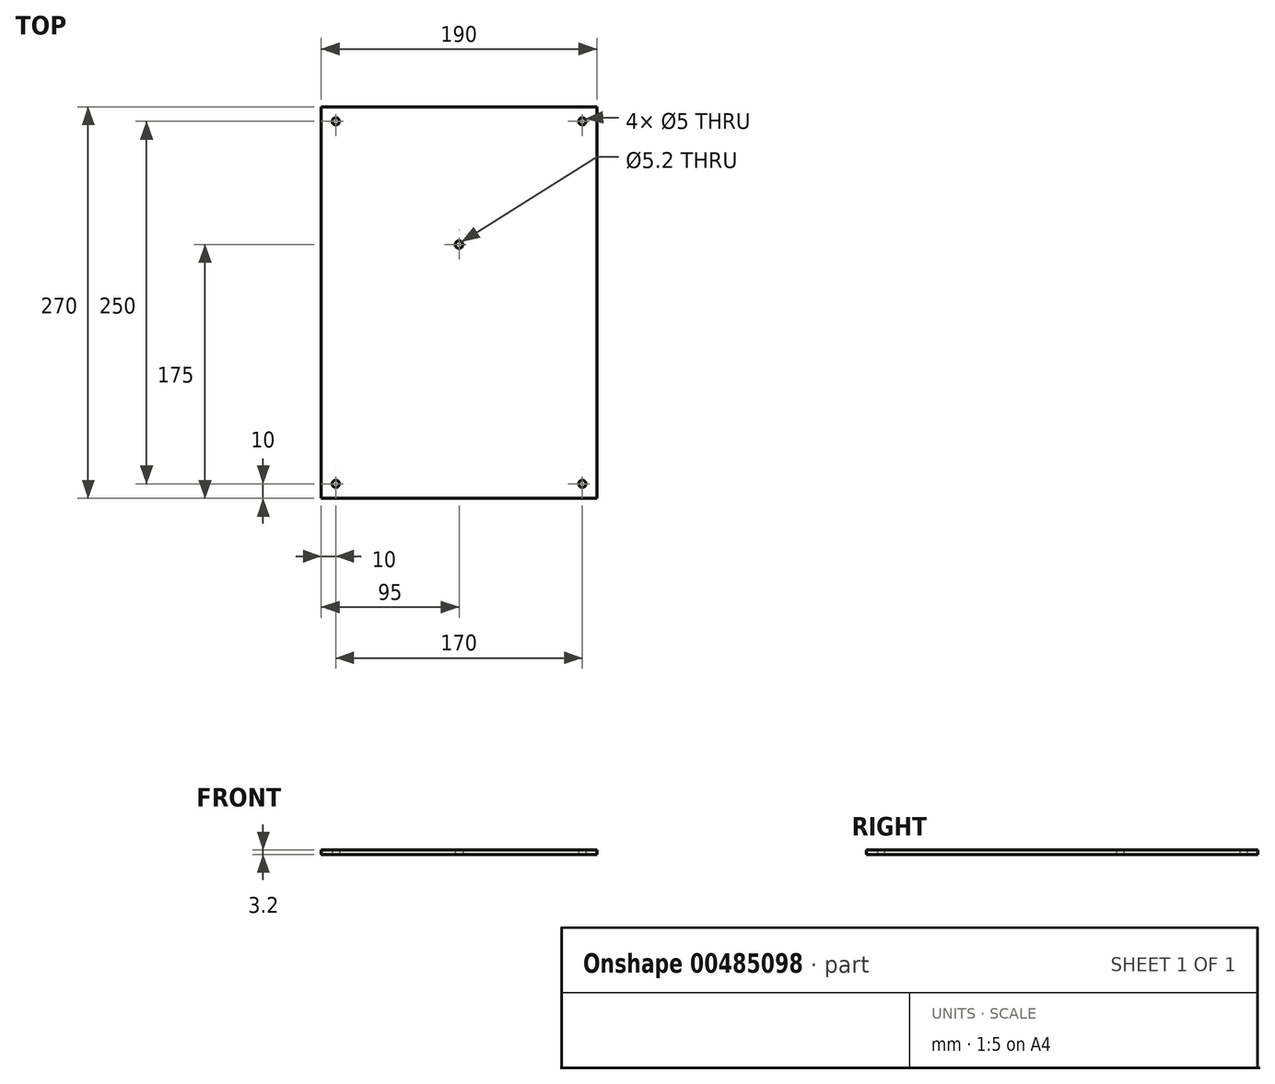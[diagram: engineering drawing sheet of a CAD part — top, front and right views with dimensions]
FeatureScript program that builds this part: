
annotation { "Feature Type Name" : "Feature", "Feature Type Description" : "" }
export const myFeature = defineFeature(function(context is Context, id is Id, definition is map)
    precondition{}
    {
        {
            var Q0;
            Q0=qCreatedBy(makeId("Top.planeOp"),FACE);
            var sketch = newSketch(context, id + "F0", { "sketchPlane" : qUnion([Q0])});
            skLineSegment(sketch, "E0.bottom", {"start": v(-95, 135) * mm, "end": v(95, 135) * mm});
            skLineSegment(sketch, "E0.top", {"start": v(-95, -135) * mm, "end": v(95, -135) * mm});
            skLineSegment(sketch, "E0.left", {"start": v(-95, 135) * mm, "end": v(-95, -135) * mm});
            skLineSegment(sketch, "E0.right", {"start": v(95, 135) * mm, "end": v(95, -135) * mm});
            skPoint(sketch, "E0.middle", {"position": v(0, 0) * mm});
            skCircle(sketch, "E1", {"center": v(-85, -125) * mm, "radius": 2.5 * mm});
            skCircle(sketch, "E2", {"center": v(-85, 125) * mm, "radius": 2.5 * mm});
            skCircle(sketch, "E3", {"center": v(85, 125) * mm, "radius": 2.5 * mm});
            skCircle(sketch, "E4", {"center": v(85, -125) * mm, "radius": 2.5 * mm});
            skLineSegment(sketch, "E5", {"start": v(-95, 40) * mm, "end": v(95, 40) * mm, "construction": true});
            skLineSegment(sketch, "E6", {"start": v(0, 135) * mm, "end": v(0, -135) * mm, "construction": true});
            skCircle(sketch, "E7", {"center": v(0, 40) * mm, "radius": 80 * mm});
            skLineSegment(sketch, "E8", {"start": v(-69.28, 80) * mm, "end": v(69.28, 80) * mm, "construction": true});
            skLineSegment(sketch, "E9", {"start": v(-69.28, 0) * mm, "end": v(69.28, 0) * mm, "construction": true});
            skCircle(sketch, "E10", {"center": v(0, 40) * mm, "radius": 2.6 * mm});
            skSolve(sketch);
        }
        {
            var Q0;
            Q0=makeQuery(id+"F0.imprint","IMPRINT",FACE,{"disambiguationData":[TD([[makeQuery(id+"F0.imprint","IMPRINT",EDGE,{"derivedFrom":sQuery(id+"F0.wireOp",EDGE,"E0.bottom")}),-1.0]])]});
            var Q1;
            Q1=makeQuery(id+"F0.imprint","IMPRINT",FACE,{"disambiguationData":[TD([[makeQuery(id+"F0.imprint","IMPRINT",EDGE,{"derivedFrom":sQuery(id+"F0.wireOp",EDGE,"7sevgCVw-3VQA-PXdj-X2Id-GUKon9O2GLyd")}),1.0]])]});
            var Q2;
            Q2=makeQuery(id+"F0.imprint","IMPRINT",FACE,{"disambiguationData":[TD([[makeQuery(id+"F0.imprint","IMPRINT",EDGE,{"derivedFrom":sQuery(id+"F0.wireOp",EDGE,"E7")}),1.0]])]});
            extrude(context, id + "F1", {"entities" : qUnion([Q0, Q1, Q2]), "depth" : 3.2 * mm, "offsetDistance" : 25 * mm});
        }
    });
